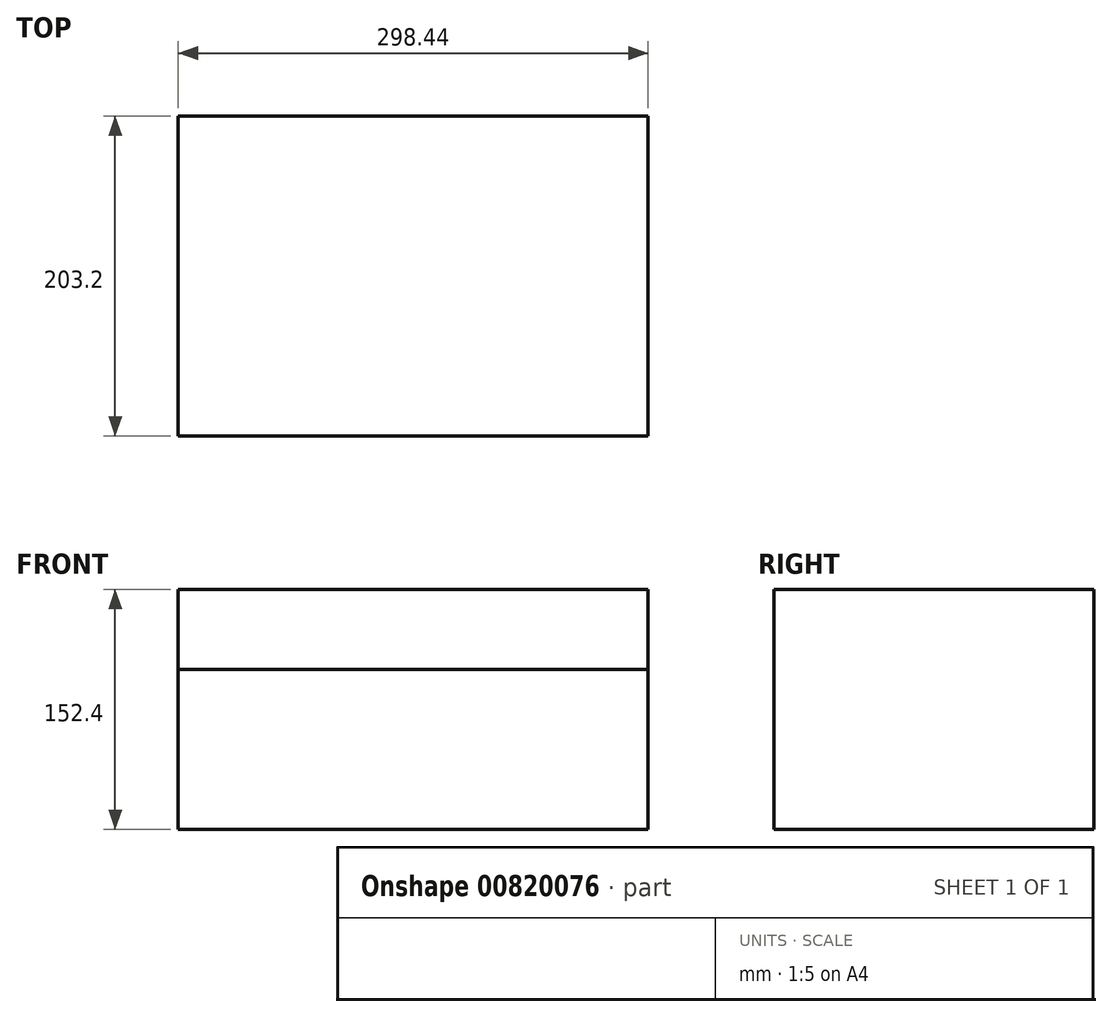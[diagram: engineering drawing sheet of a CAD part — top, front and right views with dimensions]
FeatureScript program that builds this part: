
annotation { "Feature Type Name" : "Feature", "Feature Type Description" : "" }
export const myFeature = defineFeature(function(context is Context, id is Id, definition is map)
    precondition{}
    {
        {
            var Q0;
            Q0=qCreatedBy(makeId("Front.planeOp"),FACE);
            var sketch = newSketch(context, id + "F0", { "sketchPlane" : qUnion([Q0])});
            skLineSegment(sketch, "E0.bottom", {"start": v(-149.22, -76.2) * mm, "end": v(149.23, -76.2) * mm});
            skLineSegment(sketch, "E0.top", {"start": v(-149.22, 76.2) * mm, "end": v(149.23, 76.2) * mm});
            skLineSegment(sketch, "E0.left", {"start": v(-149.22, -76.2) * mm, "end": v(-149.22, 76.2) * mm});
            skLineSegment(sketch, "E0.right", {"start": v(149.23, -76.2) * mm, "end": v(149.23, 76.2) * mm});
            skLineSegment(sketch, "E1", {"start": v(-149.22, -76.2) * mm, "end": v(149.23, 76.2) * mm, "construction": true});
            skPoint(sketch, "E2", {"position": v(0, 0) * mm});
            skSolve(sketch);
        }
        {
            var Q0;
            Q0=makeQuery(id+"F0.imprint","IMPRINT",FACE,{"disambiguationData":[TD([[makeQuery(id+"F0.imprint","IMPRINT",EDGE,{"derivedFrom":sQuery(id+"F0.wireOp",EDGE,"E0.bottom")}),1.0]])]});
            extrude(context, id + "F1", {"entities" : qUnion([Q0]), "endBound" : BoundingType.SYMMETRIC, "depth" : 203.2 * mm, "offsetDistance" : 25.4 * mm});
        }
        {
            var Q0;
            Q0=makeQuery(id+"F1.opExtrude","CAP_FACE",FACE,{"disambiguationData":[OSD([sQuery(id+"F0.wireOp",EDGE,"E0.bottom"),sQuery(id+"F0.wireOp",EDGE,"E0.top"),sQuery(id+"F0.wireOp",EDGE,"E0.left"),sQuery(id+"F0.wireOp",EDGE,"E0.right")])],"isStart":false});
            var sketch = newSketch(context, id + "F2", { "sketchPlane" : qUnion([Q0])});
            skLineSegment(sketch, "E3.bottom", {"start": v(-149.22, -76.2) * mm, "end": v(149.23, -76.2) * mm});
            skLineSegment(sketch, "E3.top", {"start": v(-149.22, 25.4) * mm, "end": v(149.23, 25.4) * mm});
            skLineSegment(sketch, "E3.left", {"start": v(-149.22, -76.2) * mm, "end": v(-149.22, 25.4) * mm});
            skLineSegment(sketch, "E3.right", {"start": v(149.23, -76.2) * mm, "end": v(149.23, 25.4) * mm});
            skSolve(sketch);
        }
        {
            var Q0;
            Q0=makeQuery(id+"F2.imprint","IMPRINT",FACE,{"disambiguationData":[TD([[makeQuery(id+"F2.imprint","IMPRINT",EDGE,{"derivedFrom":sQuery(id+"F2.wireOp",EDGE,"E3.bottom")}),1.0]])]});
            extrude(context, id + "F3", {"entities" : qUnion([Q0]), "depth" : 1 / 406.4 * mm, "offsetDistance" : 25.4 * mm});
        }
    });
